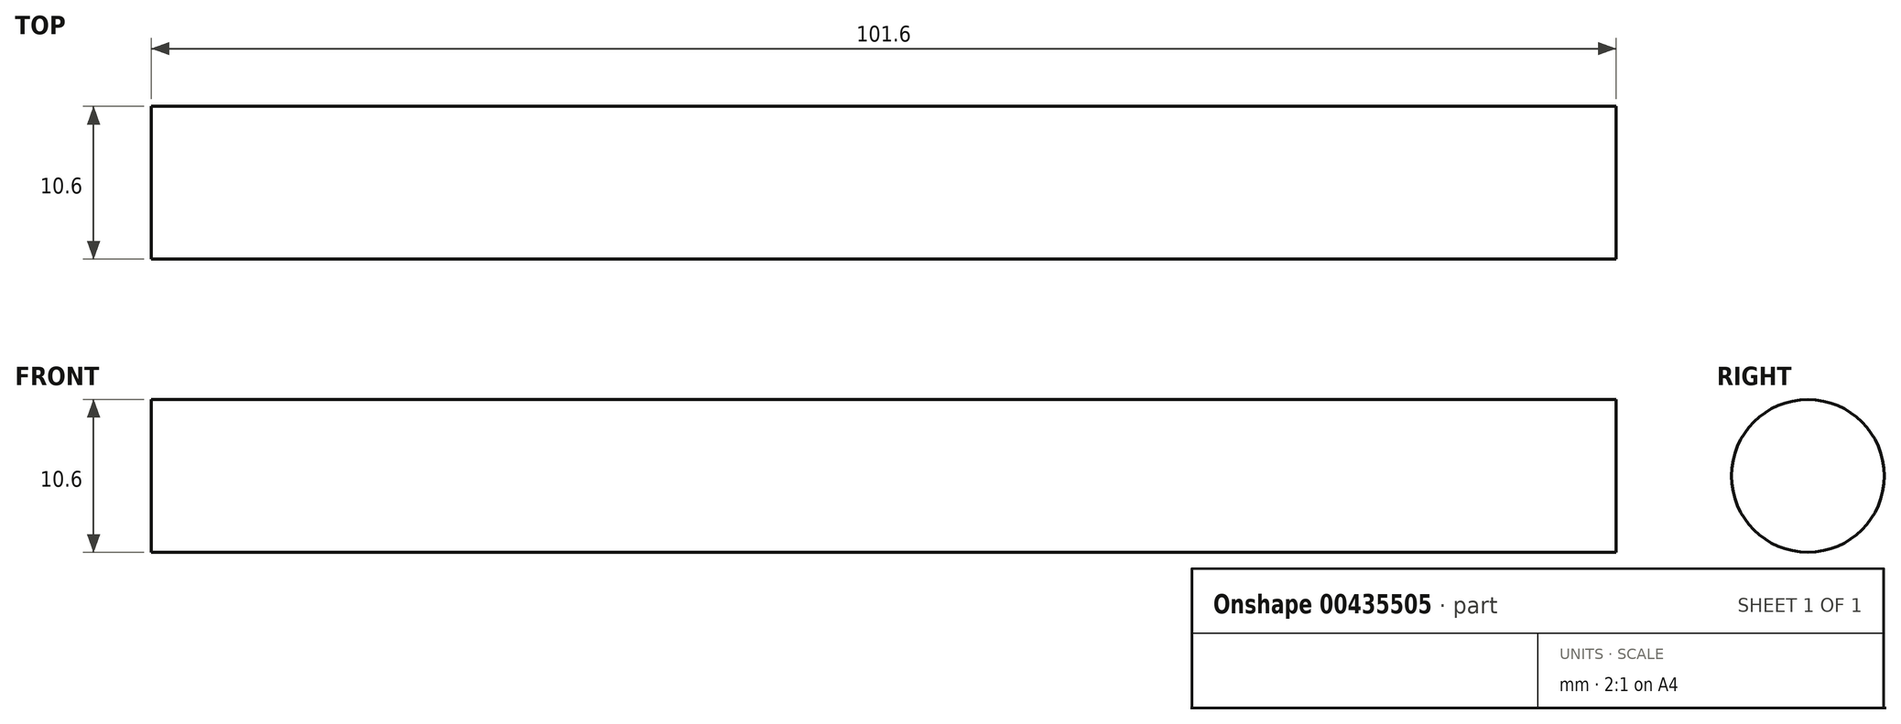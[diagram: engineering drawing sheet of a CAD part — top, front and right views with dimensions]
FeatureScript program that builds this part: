
annotation { "Feature Type Name" : "Feature", "Feature Type Description" : "" }
export const myFeature = defineFeature(function(context is Context, id is Id, definition is map)
    precondition{}
    {
        {
            var Q0;
            Q0=qCreatedBy(makeId("Right.planeOp"),FACE);
            var sketch = newSketch(context, id + "F0", { "sketchPlane" : qUnion([Q0])});
            skCircle(sketch, "E0", {"center": v(0, 0) * mm, "radius": 5.3 * mm});
            skSolve(sketch);
        }
        {
            var Q0;
            Q0 = qSketchRegion(id + "F0", true);
            extrude(context, id + "F1", {"entities" : qUnion([Q0]), "depth" : 101.6 * mm});
        }
    });
